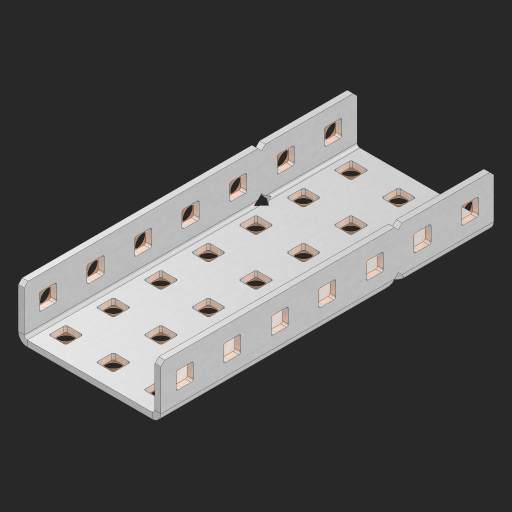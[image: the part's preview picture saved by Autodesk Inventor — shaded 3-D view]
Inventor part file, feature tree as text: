
AUTODESK INVENTOR PART (.ipt)
format: ipt  version: 2023 (Build 270158000, 158)  size: 783,872 bytes
history: native  units: in
note: dims shown in document units (in); Inventor stores cm internally (conversion verified against a paired STEP export)
features: other x40, extrude x34, sheet_metal_op x10, sketch x8, mirror x1, pattern_linear x1, chamfer x1
ambient origin geometry x8: Origin, YZ Plane, XZ Plane, XY Plane, X Axis, Y Axis, Z Axis, Center Point
bodies: Solid1 (feature_tree), Body (feature_tree)
feature tree (95):
  other  "Flange Pattern Plane"
  sheet_metal_op  "Flange Pattern"
  sheet_metal_op  "Body Pattern"
  other  "Arc Length"
  mirror  "Notch Mirror"
  pattern_linear  "Notch Pattern"  Spacing1=0.25in  [1 undecoded]
  chamfer  "End Chamfer"
  extrude  "Half Cut"  Depth=0.0625in
  sketch  "Sketch1"  dims[d0=1.5in]
  other  "Plate1"
  sketch  "Sketch2"  dims[d1=3.5in]
  other  "Plate2"
  sheet_metal_op  "Bend1"
  sheet_metal_op  "Corner1"
  sketch  "Sketch3"  dims[d2=0.0625in]
  other  "Flange Pattern Sketch"
  sketch  "Sketch7"  dims[d3=0.0625in]
  other  "Srf1"
  other  "Srf2"
  sketch  "Sketch8"  dims[d4=0.0312in]
  sketch  "Sketch9"  dims[d5=0.125in]
  other  "Srf91"
  sheet_metal_op  "Body Pattern Sketch"
  other  "Srf92"
  sketch  "Sketch13"  dims[d6=0.0625in]
  sketch  "Sketch14"  dims[d7=0.5in d8=90.0deg d9=0.0312in d10=0.25in d11=0.0625in d12=0.0625in d16=0.182in d17=0.02in d18=0.0625in d19=0.0in d20=0.25in d21=0.25in d46=0.172in d47=1.0in d48=0.0in d49=0.182in d50=0.02in d51=0.25in d52=0.25in d53=0.0625in d54=0.0in d55=0.172in d56=1.0in d57=0.0in d60=2.7559in d62=0.5in d63=1.1811in d65=0.5in d85=0.1473in d86=0.1782in d88=0.04in d89=0.0625in d90=0.0in d91=0.04in d92=0.0491in d95=2.5in d96=0.04in d97=0.25in d98=45.0deg d101=0.0in d102=2.497in d131=1.5in d132=2.7559in d134=0.5in d139=0.5in]
  other  "Srf856"
  other  "Srf1310"
  other  "Srf1311"
  other  "Srf1312"
  other  "Srf1376"
  other  "Srf1377"
  other  "Srf1728"
  other  "Srf1755"
  other  "Srf1878"
  other  "Srf1879"
  other  "Srf1880"
  other  "Srf1881"
  other  "Srf1882"
  other  "Srf1883"
  other  "Srf1884"
  other  "Srf1885"
  other  "Srf1942"
  other  "Srf1943"
  other  "Srf1944"
  other  "Srf1945"
  other  "Srf1946"
  other  "Srf1947"
  other  "Srf1948"
  other  "Srf1949"
  other  "Srf1950"
  other  "Srf1951"
  other  "Srf1952"
  other  "Srf1953"
  other  "Srf1954"
  other  "Srf1955"
  other  "Srf1956"
  sheet_metal_op  "Flange Stamp"
  sheet_metal_op  "Flange Circle"
  sheet_metal_op  "Body Stamp"
  sheet_metal_op  "Body Circle"
  sheet_metal_op  "Notch"
  extrude  "ExtrusionSrf2"  Depth=0.0625in
  extrude  "ExtrusionSrf92"  Depth=1.5in
  extrude  "ExtrusionSrf856"  Depth=0.02in
  extrude  "ExtrusionSrf1310"  Depth=0.0625in
  extrude  "ExtrusionSrf1311"  TaperAngle=0.0deg  [1 undecoded]
  extrude  "ExtrusionSrf1312"  Depth=0.25in
  extrude  "ExtrusionSrf1376"  Depth=0.25in
  extrude  "ExtrusionSrf1377"  Depth=1.5in
  extrude  "ExtrusionSrf1728"  Depth=1.5in TaperAngle=0.0deg
  extrude  "ExtrusionSrf1755"  Depth=1.5in
  extrude  "ExtrusionSrf1878"  Depth=0.02in
  extrude  "ExtrusionSrf1879"  Depth=0.25in
  extrude  "ExtrusionSrf1880"  Depth=0.25in
  extrude  "ExtrusionSrf1881"  Depth=0.0625in
  extrude  "ExtrusionSrf1882"  TaperAngle=0.0deg  [1 undecoded]
  extrude  "ExtrusionSrf1883"  Depth=1.5in
  extrude  "ExtrusionSrf1884"  Depth=1.5in TaperAngle=0.0deg
  extrude  "ExtrusionSrf1885"  Depth=1.5in
  extrude  "ExtrusionSrf1942"  Depth=1.5in
  extrude  "ExtrusionSrf1943"  Depth=1.5in
  extrude  "ExtrusionSrf1944"  Depth=1.5in
  extrude  "ExtrusionSrf1945"  Depth=1.5in
  extrude  "ExtrusionSrf1946"  Depth=0.0625in
  extrude  "ExtrusionSrf1947"  TaperAngle=0.0deg  [1 undecoded]
  extrude  "ExtrusionSrf1948"  Depth=1.5in
  extrude  "ExtrusionSrf1949"  Depth=1.5in
  extrude  "ExtrusionSrf1950"  Depth=1.5in
  extrude  "ExtrusionSrf1951"  Depth=0.25in TaperAngle=45.0deg
  extrude  "ExtrusionSrf1952"  TaperAngle=0.0deg  [1 undecoded]
  extrude  "ExtrusionSrf1953"  Depth=1.5in
  extrude  "ExtrusionSrf1954"  Depth=1.5in
  extrude  "ExtrusionSrf1955"  Depth=1.5in
  extrude  "ExtrusionSrf1956"  Depth=1.5in
note: 5 required parameter values undecoded (feature->parameter linkage not recoverable at this tier; creation-order binding heuristic only, values carry confidence <= 0.55)
